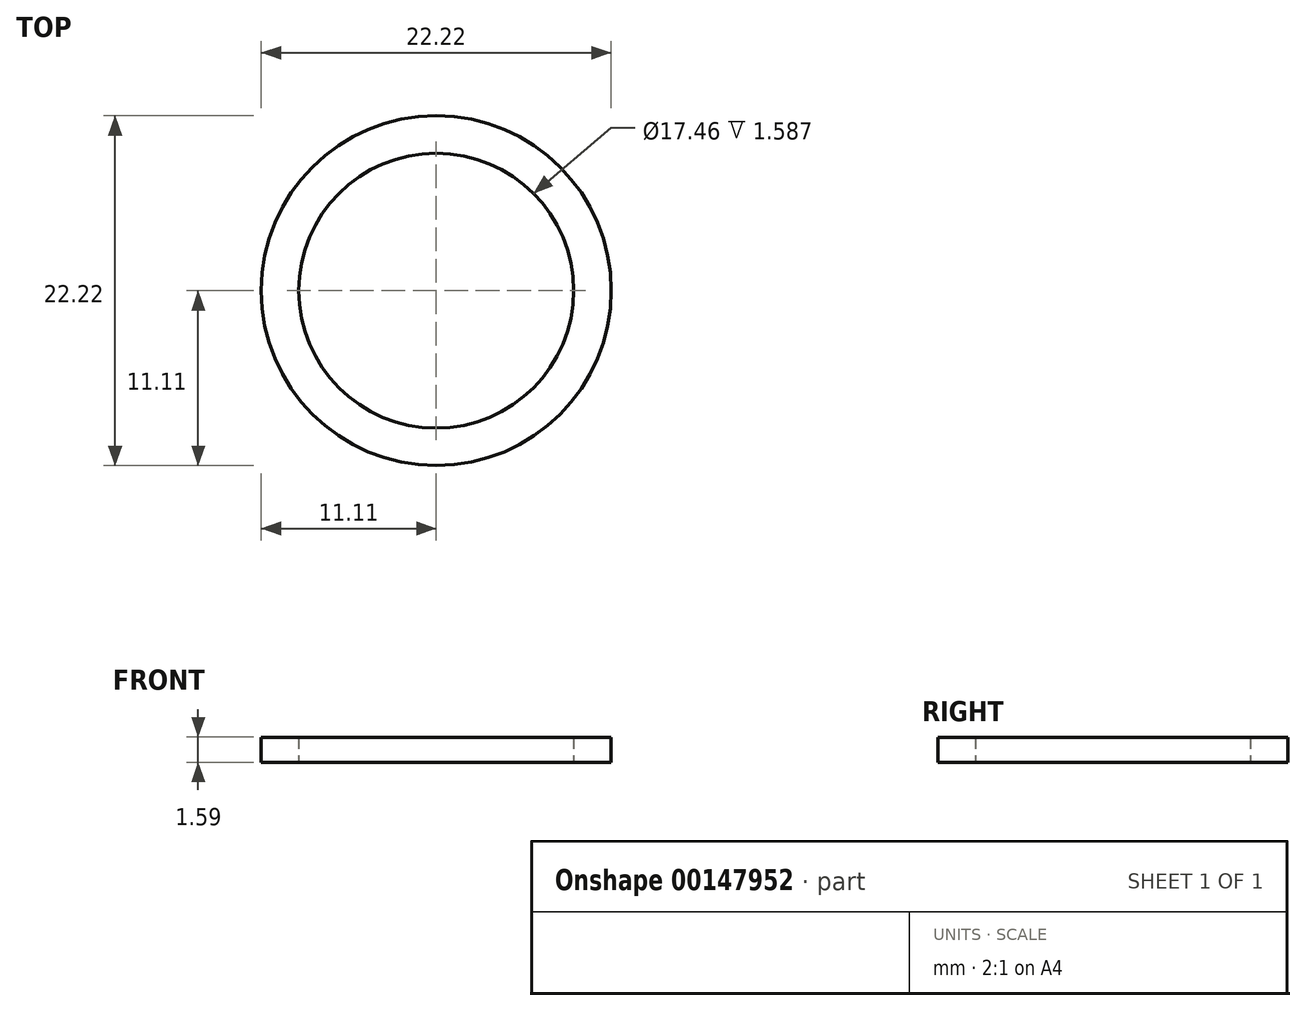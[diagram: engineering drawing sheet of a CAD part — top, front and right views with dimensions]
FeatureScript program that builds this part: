
annotation { "Feature Type Name" : "Feature", "Feature Type Description" : "" }
export const myFeature = defineFeature(function(context is Context, id is Id, definition is map)
    precondition{}
    {
        {
            var Q0;
            Q0=qCreatedBy(makeId("Top.planeOp"),FACE);
            var sketch = newSketch(context, id + "F0", { "sketchPlane" : qUnion([Q0])});
            skCircle(sketch, "E0", {"center": v(0, 0) * mm, "radius": 11.11 * mm});
            skCircle(sketch, "E1", {"center": v(0, 0) * mm, "radius": 8.73 * mm});
            skSolve(sketch);
        }
        {
            var Q0;
            Q0=qSketchRegion(id+"F0",true);
            extrude(context, id + "F1", {"entities" : qUnion([Q0]), "depth" : 1.59 * mm});
        }
    });
